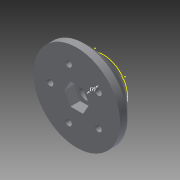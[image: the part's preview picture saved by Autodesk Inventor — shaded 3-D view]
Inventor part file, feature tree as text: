
AUTODESK INVENTOR PART (.ipt)
format: ipt  version: 2014 SP2 (Build 180246200, 246)  size: 207,360 bytes
history: native  units: mm
features: sketch x4, extrude x3, chamfer x2, fillet x1
ambient origin geometry x8: Origin, YZ Plane, XZ Plane, XY Plane, X Axis, Y Axis, Z Axis, Center Point
bodies: Solid1 (feature_tree)
feature tree (10):
  extrude  "Extrusion1"  Depth=22.2mm
  extrude  "Extrusion3"  Depth=2.7mm
  extrude  "Extrusion4"  Depth=2.7mm
  chamfer  "Chamfer2"  Distance=11.0mm
  sketch  "Sketch5"  dims[d6=2.7mm d7=11.0mm d8=0.0mm d23=9.0mm d24=4.0mm d25=0.0mm d26=6.0mm d27=17.0mm d28=0.0mm d32=8.0mm d33=2.0mm d34=45.0deg d35=7.0mm d36=3.46mm d37=2.0mm d38=45.0deg d39=14.0mm]
  chamfer  "Chamfer3"  Distance=9.0mm
  fillet  "Fillet3"  Radius=4.0mm
  sketch  "Sketch1"  dims[d0=36.0mm d1=22.2mm]
  sketch  "Sketch3"  dims[d2=2.7mm d3=2.7mm]
  sketch  "Sketch4"  dims[d4=2.7mm d5=2.7mm]
